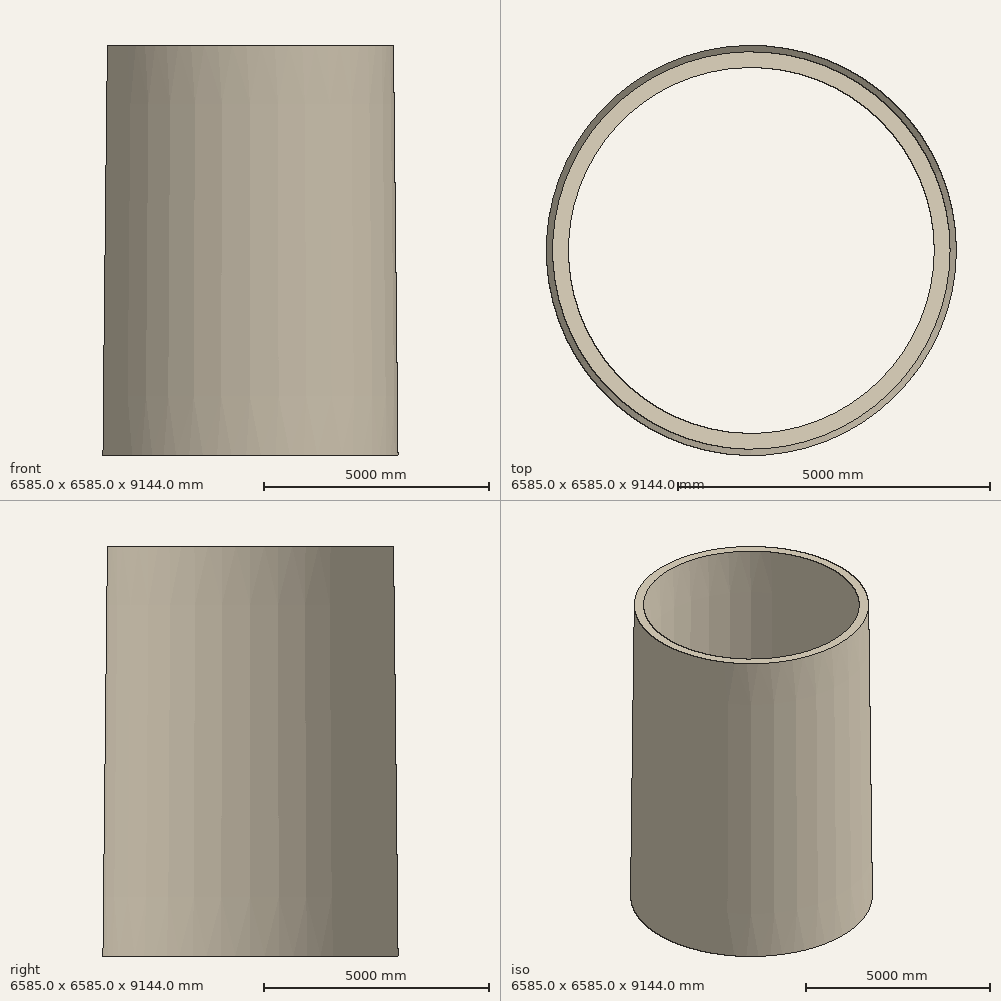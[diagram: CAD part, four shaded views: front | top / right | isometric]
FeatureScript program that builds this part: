
annotation { "Feature Type Name" : "Feature", "Feature Type Description" : "" }
export const myFeature = defineFeature(function(context is Context, id is Id, definition is map)
    precondition{}
    {
        {
            var Q0;
            Q0=qCreatedBy(makeId("Top.planeOp"),FACE);
            var sketch = newSketch(context, id + "F0", { "sketchPlane" : qUnion([Q0])});
            skCircle(sketch, "E0.0", {"center": v(0, 0) * mm, "radius": 3292.47 * mm});
            skSolve(sketch);
        }
        {
            var Q0;
            Q0=makeQuery(id+"F0.imprint","IMPRINT",FACE,{"disambiguationData":[TD([[makeQuery(id+"F0.imprint","IMPRINT",EDGE,{"derivedFrom":sQuery(id+"F0.wireOp",EDGE,"E0.0")}),1.0]])]});
            cPlane(context, id + "F1", {"entities" : qUnion([Q0]), "cplaneType" : CPlaneType.OFFSET, "offset" : 2286 * mm, "width" : 152.4 * mm, "height" : 152.4 * mm});
        }
        {
            var Q0;
            Q0=qCreatedBy(id+"F1.planeOp",FACE);
            var sketch = newSketch(context, id + "F2", { "sketchPlane" : qUnion([Q0])});
            skCircle(sketch, "E1.0", {"center": v(0, 0) * mm, "radius": 3267.08 * mm});
            skSolve(sketch);
        }
        {
            var Q0;
            Q0=makeQuery(id+"F0.imprint","IMPRINT",FACE,{"disambiguationData":[TD([[makeQuery(id+"F0.imprint","IMPRINT",EDGE,{"derivedFrom":sQuery(id+"F0.wireOp",EDGE,"E0.0")}),1.0]])]});
            var Q1;
            Q1=makeQuery(id+"F2.imprint","IMPRINT",FACE,{"disambiguationData":[TD([[makeQuery(id+"F2.imprint","IMPRINT",EDGE,{"derivedFrom":sQuery(id+"F2.wireOp",EDGE,"E1.0")}),1.0]])]});
            loft(context, id + "F3", {"sheetProfilesArray" : [{ "sheetProfileEntities" : qUnion([Q0]) }, { "sheetProfileEntities" : qUnion([Q1]) }]});
        }
        {
            var Q0;
            Q0=makeQuery(id+"F3.opLoft","CAP_FACE",FACE,{"disambiguationData":[OSD([makeQuery(id+"F0.imprint","IMPRINT",FACE,{"disambiguationData":[TD([[makeQuery(id+"F0.imprint","IMPRINT",EDGE,{"derivedFrom":sQuery(id+"F0.wireOp",EDGE,"E0.0")}),1.0]])]})])],"isStart":true});
            var Q1;
            Q1=makeQuery(id+"F3.opLoft","CAP_FACE",FACE,{"disambiguationData":[OSD([makeQuery(id+"F2.imprint","IMPRINT",FACE,{"disambiguationData":[TD([[makeQuery(id+"F2.imprint","IMPRINT",EDGE,{"derivedFrom":sQuery(id+"F2.wireOp",EDGE,"E1.0")}),1.0]])]})])],"isStart":true});
            shell(context, id + "F4", {"entities" : qUnion([Q0, Q1]), "thickness" : 254 * mm});
        }
        {
            var Q0;
            Q0=qCreatedBy(id+"F1.planeOp",FACE);
            var sketch = newSketch(context, id + "F5", { "sketchPlane" : qUnion([Q0])});
            skCircle(sketch, "E2.0", {"center": v(0, 0) * mm, "radius": 3267.08 * mm});
            skSolve(sketch);
        }
        {
            var Q0;
            Q0=qCreatedBy(id+"F1.planeOp",FACE);
            cPlane(context, id + "F6", {"entities" : qUnion([Q0]), "cplaneType" : CPlaneType.OFFSET, "offset" : 2286 * mm, "width" : 152.4 * mm, "height" : 152.4 * mm});
        }
        {
            var Q0;
            Q0=qCreatedBy(id+"F6.planeOp",FACE);
            var sketch = newSketch(context, id + "F7", { "sketchPlane" : qUnion([Q0])});
            skCircle(sketch, "E3.0", {"center": v(0, 0) * mm, "radius": 3241.67 * mm});
            skSolve(sketch);
        }
        {
            var Q1;
            Q1=makeQuery(id+"F5.imprint","IMPRINT",FACE,{"disambiguationData":[TD([[makeQuery(id+"F5.imprint","IMPRINT",EDGE,{"derivedFrom":sQuery(id+"F5.wireOp",EDGE,"E2.0")}),1.0]])]});
            var Q2;
            Q2=makeQuery(id+"F7.imprint","IMPRINT",FACE,{"disambiguationData":[TD([[makeQuery(id+"F7.imprint","IMPRINT",EDGE,{"derivedFrom":sQuery(id+"F7.wireOp",EDGE,"E3.0")}),1.0]])]});
            loft(context, id + "F8", {"operationType" : NewBodyOperationType.ADD, "sheetProfilesArray" : [{ "sheetProfileEntities" : qUnion([Q1]) }, { "sheetProfileEntities" : qUnion([Q2]) }]});
        }
        {
            var Q0;
            Q0=makeQuery(id+"F8.opLoft","CAP_FACE",FACE,{"disambiguationData":[OSD([makeQuery(id+"F5.imprint","IMPRINT",FACE,{"disambiguationData":[TD([[makeQuery(id+"F5.imprint","IMPRINT",EDGE,{"derivedFrom":sQuery(id+"F5.wireOp",EDGE,"E2.0")}),1.0]])]})])],"isStart":true});
            var Q1;
            Q1=makeQuery(id+"F8.opLoft","CAP_FACE",FACE,{"disambiguationData":[OSD([makeQuery(id+"F7.imprint","IMPRINT",FACE,{"disambiguationData":[TD([[makeQuery(id+"F7.imprint","IMPRINT",EDGE,{"derivedFrom":sQuery(id+"F7.wireOp",EDGE,"E3.0")}),1.0]])]})])],"isStart":true});
            shell(context, id + "F9", {"entities" : qUnion([Q0, Q1]), "thickness" : 254 * mm});
        }
        {
            var Q0;
            Q0=qCreatedBy(id+"F6.planeOp",FACE);
            var sketch = newSketch(context, id + "F10", { "sketchPlane" : qUnion([Q0])});
            skCircle(sketch, "E4.0", {"center": v(0, 0) * mm, "radius": 3241.67 * mm});
            skSolve(sketch);
        }
        {
            var Q0;
            Q0=qCreatedBy(id+"F6.planeOp",FACE);
            cPlane(context, id + "F11", {"entities" : qUnion([Q0]), "cplaneType" : CPlaneType.OFFSET, "offset" : 2286 * mm, "width" : 152.4 * mm, "height" : 152.4 * mm});
        }
        {
            var Q0;
            Q0=qCreatedBy(id+"F11.planeOp",FACE);
            var sketch = newSketch(context, id + "F12", { "sketchPlane" : qUnion([Q0])});
            skCircle(sketch, "E5.0", {"center": v(0, 0) * mm, "radius": 3216.28 * mm});
            skSolve(sketch);
        }
        {
            var Q1;
            Q1=makeQuery(id+"F10.imprint","IMPRINT",FACE,{"disambiguationData":[TD([[makeQuery(id+"F10.imprint","IMPRINT",EDGE,{"derivedFrom":sQuery(id+"F10.wireOp",EDGE,"E4.0")}),1.0]])]});
            var Q2;
            Q2=makeQuery(id+"F12.imprint","IMPRINT",FACE,{"disambiguationData":[TD([[makeQuery(id+"F12.imprint","IMPRINT",EDGE,{"derivedFrom":sQuery(id+"F12.wireOp",EDGE,"E5.0")}),1.0]])]});
            loft(context, id + "F13", {"operationType" : NewBodyOperationType.ADD, "sheetProfilesArray" : [{ "sheetProfileEntities" : qUnion([Q1]) }, { "sheetProfileEntities" : qUnion([Q2]) }]});
        }
        {
            var Q0;
            Q0=makeQuery(id+"F13.opLoft","CAP_FACE",FACE,{"disambiguationData":[OSD([makeQuery(id+"F12.imprint","IMPRINT",FACE,{"disambiguationData":[TD([[makeQuery(id+"F12.imprint","IMPRINT",EDGE,{"derivedFrom":sQuery(id+"F12.wireOp",EDGE,"E5.0")}),1.0]])]})])],"isStart":true});
            var Q1;
            Q1=makeQuery(id+"F13.opLoft","CAP_FACE",FACE,{"disambiguationData":[OSD([makeQuery(id+"F10.imprint","IMPRINT",FACE,{"disambiguationData":[TD([[makeQuery(id+"F10.imprint","IMPRINT",EDGE,{"derivedFrom":sQuery(id+"F10.wireOp",EDGE,"E4.0")}),1.0]])]})])],"isStart":true});
            shell(context, id + "F14", {"entities" : qUnion([Q0, Q1]), "thickness" : 254 * mm});
        }
        {
            var Q0;
            Q0=qCreatedBy(id+"F11.planeOp",FACE);
            var sketch = newSketch(context, id + "F15", { "sketchPlane" : qUnion([Q0])});
            skCircle(sketch, "E6.0", {"center": v(0, 0) * mm, "radius": 3216.28 * mm});
            skSolve(sketch);
        }
        {
            var Q0;
            Q0=qCreatedBy(id+"F11.planeOp",FACE);
            cPlane(context, id + "F16", {"entities" : qUnion([Q0]), "cplaneType" : CPlaneType.OFFSET, "offset" : 2286 * mm, "width" : 152.4 * mm, "height" : 152.4 * mm});
        }
        {
            var Q0;
            Q0=qCreatedBy(id+"F16.planeOp",FACE);
            var sketch = newSketch(context, id + "F17", { "sketchPlane" : qUnion([Q0])});
            skCircle(sketch, "E7", {"center": v(0, 0) * mm, "radius": 3190.88 * mm});
            skSolve(sketch);
        }
        {
            var Q1;
            Q1=makeQuery(id+"F15.imprint","IMPRINT",FACE,{"disambiguationData":[TD([[makeQuery(id+"F15.imprint","IMPRINT",EDGE,{"derivedFrom":sQuery(id+"F15.wireOp",EDGE,"E6.0")}),1.0]])]});
            var Q2;
            Q2=makeQuery(id+"F17.imprint","IMPRINT",FACE,{"disambiguationData":[TD([[makeQuery(id+"F17.imprint","IMPRINT",EDGE,{"derivedFrom":sQuery(id+"F17.wireOp",EDGE,"E7")}),1.0]])]});
            loft(context, id + "F18", {"operationType" : NewBodyOperationType.ADD, "sheetProfilesArray" : [{ "sheetProfileEntities" : qUnion([Q1]) }, { "sheetProfileEntities" : qUnion([Q2]) }]});
        }
        {
            var Q0;
            Q0=makeQuery(id+"F18.opLoft","CAP_FACE",FACE,{"disambiguationData":[OSD([makeQuery(id+"F15.imprint","IMPRINT",FACE,{"disambiguationData":[TD([[makeQuery(id+"F15.imprint","IMPRINT",EDGE,{"derivedFrom":sQuery(id+"F15.wireOp",EDGE,"E6.0")}),1.0]])]})])],"isStart":true});
            var Q1;
            Q1=makeQuery(id+"F18.opLoft","CAP_FACE",FACE,{"disambiguationData":[OSD([makeQuery(id+"F17.imprint","IMPRINT",FACE,{"disambiguationData":[TD([[makeQuery(id+"F17.imprint","IMPRINT",EDGE,{"derivedFrom":sQuery(id+"F17.wireOp",EDGE,"E7")}),1.0]])]})])],"isStart":true});
            shell(context, id + "F19", {"entities" : qUnion([Q0, Q1]), "thickness" : 254 * mm});
        }
    });
